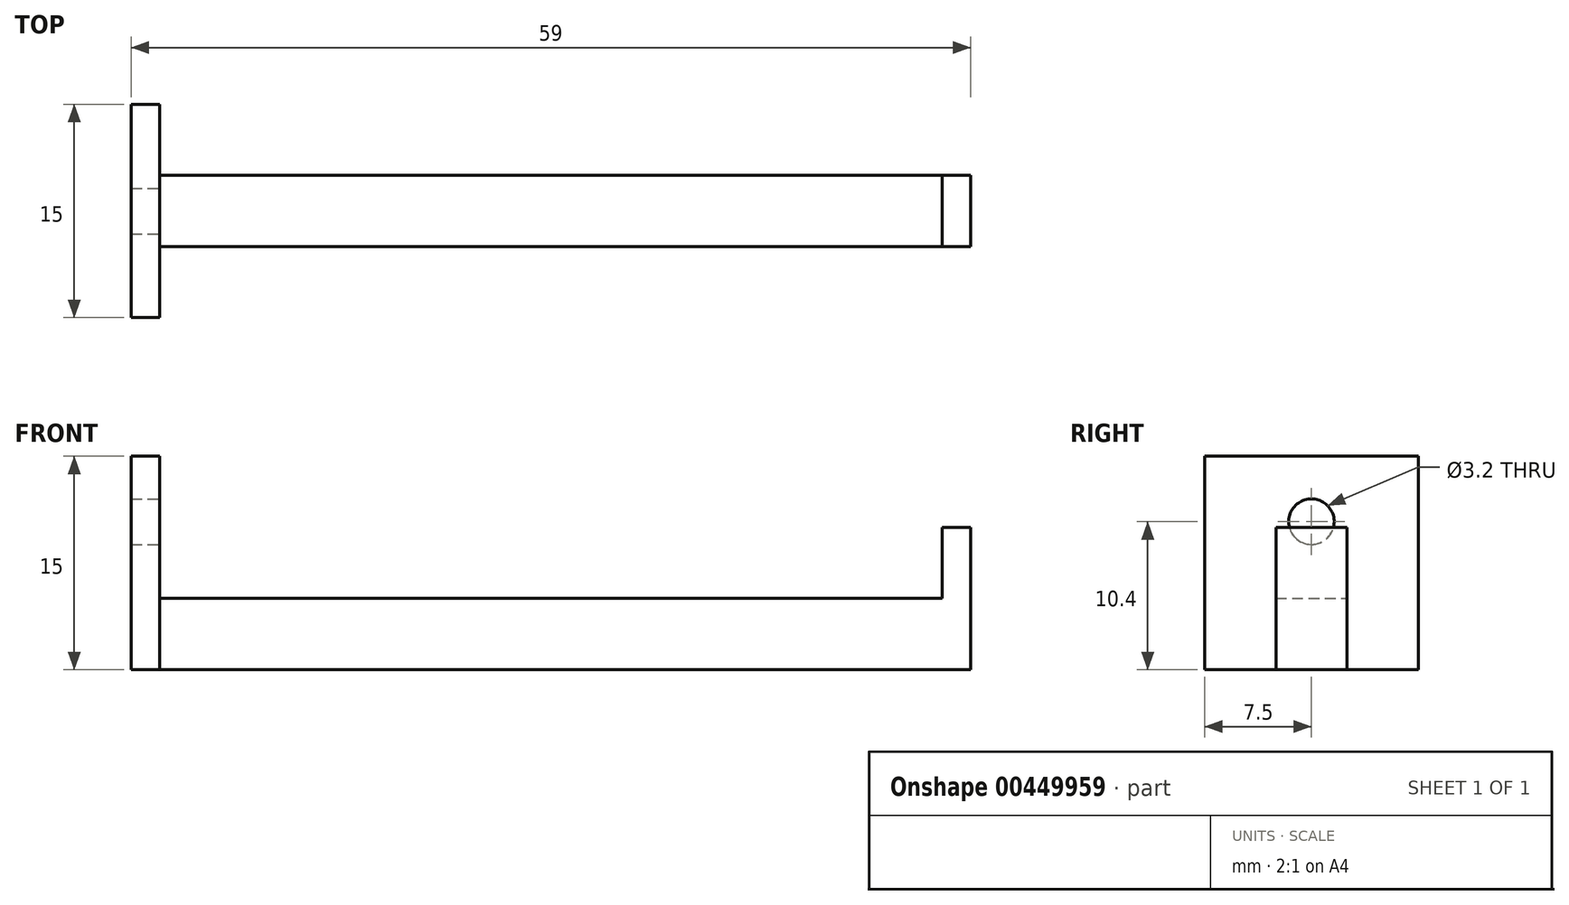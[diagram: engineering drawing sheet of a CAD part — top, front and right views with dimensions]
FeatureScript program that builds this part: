
annotation { "Feature Type Name" : "Feature", "Feature Type Description" : "" }
export const myFeature = defineFeature(function(context is Context, id is Id, definition is map)
    precondition{}
    {
        {
            var Q0;
            Q0=qCreatedBy(makeId("Front.planeOp"),FACE);
            var sketch = newSketch(context, id + "F0", { "sketchPlane" : qUnion([Q0])});
            skLineSegment(sketch, "E0.bottom", {"start": v(0, 0) * mm, "end": v(2, 0) * mm});
            skLineSegment(sketch, "E0.top", {"start": v(0, 15) * mm, "end": v(2, 15) * mm});
            skLineSegment(sketch, "E0.left", {"start": v(0, 0) * mm, "end": v(0, 15) * mm});
            skLineSegment(sketch, "E0.right", {"start": v(2, 0) * mm, "end": v(2, 15) * mm});
            skLineSegment(sketch, "E1.bottom", {"start": v(2, 0) * mm, "end": v(57, 0) * mm});
            skLineSegment(sketch, "E1.top", {"start": v(2, 5) * mm, "end": v(57, 5) * mm});
            skLineSegment(sketch, "E1.left", {"start": v(2, 0) * mm, "end": v(2, 5) * mm});
            skLineSegment(sketch, "E1.right", {"start": v(57, 0) * mm, "end": v(57, 5) * mm});
            skLineSegment(sketch, "E2.bottom", {"start": v(57, 0) * mm, "end": v(59, 0) * mm});
            skLineSegment(sketch, "E2.top", {"start": v(57, 10) * mm, "end": v(59, 10) * mm});
            skLineSegment(sketch, "E2.left", {"start": v(57, 0) * mm, "end": v(57, 10) * mm});
            skLineSegment(sketch, "E2.right", {"start": v(59, 0) * mm, "end": v(59, 10) * mm});
            skSolve(sketch);
        }
        {
            var Q0;
            {var subQ0=sQuery(id+"F0.wireOp",EDGE,"E1.bottom");Q0=makeQuery(id+"F0.imprint","IMPRINT",FACE,{"disambiguationData":[TD([[makeQuery(id+"F0.imprint","IMPRINT",EDGE,{"derivedFrom":subQ0}),1.0]])]});}
            var Q1;
            {var subQ3=sQuery(id+"F0.wireOp",EDGE,"E2.bottom");Q1=makeQuery(id+"F0.imprint","IMPRINT",FACE,{"disambiguationData":[TD([[makeQuery(id+"F0.imprint","IMPRINT",EDGE,{"derivedFrom":subQ3}),1.0]])]});}
            extrude(context, id + "F1", {"entities" : qUnion([Q0, Q1]), "depth" : 5 * mm});
        }
        {
            var Q0;
            Q0=makeQuery(id+"F0.imprint","IMPRINT",FACE,{"disambiguationData":[TD([[makeQuery(id+"F0.imprint","IMPRINT",EDGE,{"derivedFrom":sQuery(id+"F0.wireOp",EDGE,"E0.bottom")}),1.0]])]});
            extrude(context, id + "F2", {"entities" : qUnion([Q0]), "operationType" : NewBodyOperationType.ADD, "depth" : 10 * mm, "hasSecondDirection" : true, "secondDirectionOppositeDirection" : true, "secondDirectionDepth" : 5 * mm});
        }
        {
            var Q0;
            Q0=makeQuery(id+"F2.opExtrude","SWEPT_FACE",FACE,{"disambiguationData":[OSD([sQuery(id+"F0.wireOp",EDGE,"E0.right"),sQuery(id+"F0.wireOp",EDGE,"E1.left")])]});
            var sketch = newSketch(context, id + "F3", { "sketchPlane" : qUnion([Q0])});
            skCircle(sketch, "E3", {"center": v(-2.5, 10.4) * mm, "radius": 1.6 * mm});
            skSolve(sketch);
        }
        {
            var Q0;
            Q0=sQuery(id+"F3.wireOp",VERTEX,"E3.center");
            var Q1;
            Q1=makeQuery(id+"F1.opExtrude","SWEPT_BODY",BODY,{"disambiguationData":[OSD([sQuery(id+"F0.wireOp",EDGE,"E1.bottom"),sQuery(id+"F0.wireOp",EDGE,"E1.top"),sQuery(id+"F0.wireOp",EDGE,"E1.left"),sQuery(id+"F0.wireOp",EDGE,"E2.bottom"),sQuery(id+"F0.wireOp",EDGE,"E2.top"),sQuery(id+"F0.wireOp",EDGE,"E2.left"),sQuery(id+"F0.wireOp",EDGE,"E2.right")])]});
            hole(context, id + "F4", {"style" : HoleStyle.SIMPLE, "endStyle" : HoleEndStyle.THROUGH, "holeDiameter" : 3.2 * mm, "isTappedThrough" : true, "tappedDepth" : 12 * mm, "tapClearance" : 3, "locations" : qUnion([Q0]), "scope" : qUnion([Q1])});
        }
    });
